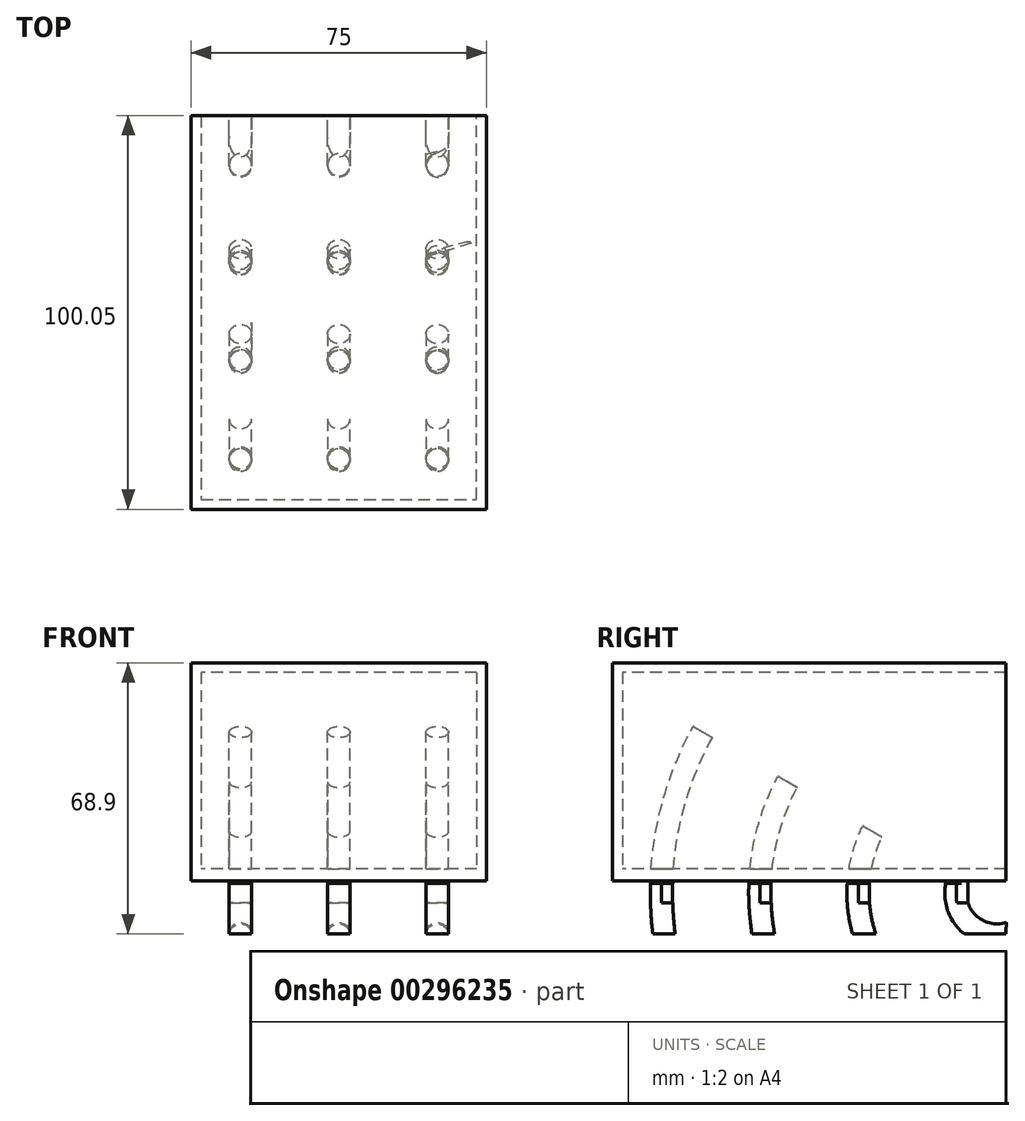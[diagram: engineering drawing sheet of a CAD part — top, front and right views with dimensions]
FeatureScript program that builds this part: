
annotation { "Feature Type Name" : "Feature", "Feature Type Description" : "" }
export const myFeature = defineFeature(function(context is Context, id is Id, definition is map)
    precondition{}
    {
        {
            var Q0;
            Q0=qCreatedBy(makeId("Top.planeOp"),FACE);
            var sketch = newSketch(context, id + "F0", { "sketchPlane" : qUnion([Q0])});
            skLineSegment(sketch, "E0.bottom", {"start": v(37.5, 50) * mm, "end": v(-37.5, 50) * mm});
            skLineSegment(sketch, "E0.top", {"start": v(37.5, -50) * mm, "end": v(-37.5, -50) * mm});
            skLineSegment(sketch, "E0.left", {"start": v(37.5, 50) * mm, "end": v(37.5, -50) * mm});
            skLineSegment(sketch, "E0.right", {"start": v(-37.5, 50) * mm, "end": v(-37.5, -50) * mm});
            skPoint(sketch, "E0.middle", {"position": v(0, 0) * mm});
            skSolve(sketch);
        }
        {
            var Q0;
            Q0 = qSketchRegion(id + "F0", true);
            extrude(context, id + "F1", {"entities" : qUnion([Q0]), "depth" : 3 * mm});
        }
        {
            var Q0;
            Q0=makeQuery(id+"F1.opExtrude","CAP_FACE",FACE,{"disambiguationData":[OSD([sQuery(id+"F0.wireOp",EDGE,"E0.bottom"),sQuery(id+"F0.wireOp",EDGE,"E0.top"),sQuery(id+"F0.wireOp",EDGE,"E0.left"),sQuery(id+"F0.wireOp",EDGE,"E0.right")])],"isStart":false});
            var sketch = newSketch(context, id + "F2", { "sketchPlane" : qUnion([Q0])});
            skLineSegment(sketch, "E1.top", {"start": v(-35, -47.5) * mm, "end": v(35, -47.5) * mm});
            skLineSegment(sketch, "E1.left", {"start": v(-35, 47.5) * mm, "end": v(-35, -47.5) * mm});
            skLineSegment(sketch, "E1.right", {"start": v(35, 47.5) * mm, "end": v(35, -47.5) * mm});
            skPoint(sketch, "E1.middle", {"position": v(0, 0) * mm});
            skLineSegment(sketch, "E2", {"start": v(-35, 47.5) * mm, "end": v(-35, 50) * mm});
            skLineSegment(sketch, "E3", {"start": v(35, 47.5) * mm, "end": v(35, 50) * mm});
            skLineSegment(sketch, "E4.bottom", {"start": v(-37.5, -50) * mm, "end": v(37.5, -50) * mm});
            skLineSegment(sketch, "E4.top", {"start": v(-37.5, 50) * mm, "end": v(37.5, 50) * mm});
            skLineSegment(sketch, "E4.left", {"start": v(-37.5, -50) * mm, "end": v(-37.5, 50) * mm});
            skLineSegment(sketch, "E4.right", {"start": v(37.5, -50) * mm, "end": v(37.5, 50) * mm});
            skSolve(sketch);
        }
        {
            var Q0;
            Q0=makeQuery(id+"F2.imprint","IMPRINT",FACE,{"disambiguationData":[TD([[makeQuery(id+"F2.imprint","IMPRINT",EDGE,{"derivedFrom":sQuery(id+"F2.wireOp",EDGE,"E1.top")}),-1.0]])]});
            extrude(context, id + "F3", {"entities" : qUnion([Q0]), "operationType" : NewBodyOperationType.ADD, "depth" : 50 * mm});
        }
        {
            var Q0;
            Q0=makeQuery(id+"F3.opExtrude","CAP_FACE",FACE,{"disambiguationData":[OSD([sQuery(id+"F2.wireOp",EDGE,"E1.top"),sQuery(id+"F2.wireOp",EDGE,"E1.left"),sQuery(id+"F2.wireOp",EDGE,"E1.right"),sQuery(id+"F2.wireOp",EDGE,"E2"),sQuery(id+"F2.wireOp",EDGE,"E3"),sQuery(id+"F2.wireOp",EDGE,"E4.bottom"),sQuery(id+"F2.wireOp",EDGE,"E4.top"),sQuery(id+"F2.wireOp",EDGE,"E4.left"),sQuery(id+"F2.wireOp",EDGE,"E4.right")])],"isStart":false});
            var sketch = newSketch(context, id + "F4", { "sketchPlane" : qUnion([Q0])});
            skLineSegment(sketch, "E5.bottom", {"start": v(-37.5, -50) * mm, "end": v(37.5, -50) * mm});
            skLineSegment(sketch, "E5.top", {"start": v(-37.5, 50) * mm, "end": v(37.5, 50) * mm});
            skLineSegment(sketch, "E5.left", {"start": v(-37.5, -50) * mm, "end": v(-37.5, 50) * mm});
            skLineSegment(sketch, "E5.right", {"start": v(37.5, -50) * mm, "end": v(37.5, 50) * mm});
            skSolve(sketch);
        }
        {
            var Q0;
            Q0 = qSketchRegion(id + "F4", true);
            extrude(context, id + "F5", {"entities" : qUnion([Q0]), "operationType" : NewBodyOperationType.ADD, "depth" : 2.4 * mm});
        }
        {
            var Q0;
            Q0=makeQuery(id+"F1.opExtrude","CAP_FACE",FACE,{"disambiguationData":[OSD([sQuery(id+"F0.wireOp",EDGE,"E0.bottom"),sQuery(id+"F0.wireOp",EDGE,"E0.top"),sQuery(id+"F0.wireOp",EDGE,"E0.left"),sQuery(id+"F0.wireOp",EDGE,"E0.right")])],"isStart":true});
            var sketch = newSketch(context, id + "F6", { "sketchPlane" : qUnion([Q0])});
            skLineSegment(sketch, "E6.bottom", {"start": v(37.5, -50) * mm, "end": v(-37.5, -50) * mm, "construction": true});
            skLineSegment(sketch, "E6.top", {"start": v(37.5, 50) * mm, "end": v(-37.5, 50) * mm, "construction": true});
            skLineSegment(sketch, "E6.left", {"start": v(37.5, -50) * mm, "end": v(37.5, 50) * mm, "construction": true});
            skLineSegment(sketch, "E6.right", {"start": v(-37.5, -50) * mm, "end": v(-37.5, 50) * mm, "construction": true});
            skLineSegment(sketch, "E7.bottom", {"start": v(-25, -37.5) * mm, "end": v(25, -37.5) * mm, "construction": true});
            skLineSegment(sketch, "E7.top", {"start": v(-25, 37.5) * mm, "end": v(25, 37.5) * mm, "construction": true});
            skLineSegment(sketch, "E7.left", {"start": v(-25, -37.5) * mm, "end": v(-25, 37.5) * mm, "construction": true});
            skLineSegment(sketch, "E7.right", {"start": v(25, -37.5) * mm, "end": v(25, 37.5) * mm, "construction": true});
            skPoint(sketch, "E7.middle", {"position": v(0, 0) * mm});
            skLineSegment(sketch, "E8", {"start": v(0, -52.67) * mm, "end": v(0, 62.06) * mm, "construction": true});
            skPoint(sketch, "E8.startSnap0", {"position": v(0, -50) * mm});
            skLineSegment(sketch, "E9", {"start": v(25, -12.5) * mm, "end": v(-25, -12.5) * mm, "construction": true});
            skLineSegment(sketch, "E10", {"start": v(25, 12.5) * mm, "end": v(-25, 12.5) * mm, "construction": true});
            skCircle(sketch, "E11", {"center": v(25, -37.5) * mm, "radius": 2.83 * mm});
            skCircle(sketch, "E12.MirrorC", {"center": v(-25, -37.5) * mm, "radius": 2.83 * mm});
            skCircle(sketch, "E13.MirrorC", {"center": v(25, 12.5) * mm, "radius": 2.83 * mm});
            skCircle(sketch, "E14.MirrorC", {"center": v(-25, 12.5) * mm, "radius": 2.83 * mm});
            skCircle(sketch, "E15", {"center": v(0, -37.5) * mm, "radius": 2.83 * mm});
            skCircle(sketch, "E16", {"center": v(0, -12.5) * mm, "radius": 2.83 * mm});
            skCircle(sketch, "E17", {"center": v(-25, -12.5) * mm, "radius": 2.83 * mm});
            skCircle(sketch, "E18", {"center": v(25, -12.5) * mm, "radius": 2.83 * mm});
            skCircle(sketch, "E19", {"center": v(25, 37.5) * mm, "radius": 2.83 * mm});
            skCircle(sketch, "E20", {"center": v(0, 37.5) * mm, "radius": 2.83 * mm});
            skCircle(sketch, "E21", {"center": v(0, 12.5) * mm, "radius": 2.83 * mm});
            skCircle(sketch, "E22", {"center": v(-25, 37.5) * mm, "radius": 2.83 * mm});
            skSolve(sketch);
        }
        {
            var Q0;
            Q0 = qSketchRegion(id + "F6", true);
            extrude(context, id + "F7", {"entities" : qUnion([Q0]), "operationType" : NewBodyOperationType.ADD, "depth" : 5.6 * mm});
        }
        {
            var Q0;
            Q0=makeQuery(id+"F5.boolean.opBoolean","MERGE",FACE,{"derivedFrom":[makeQuery(id+"F3.boolean.opBoolean","MERGE",FACE,{"derivedFrom":[makeQuery(id+"F1.opExtrude","SWEPT_FACE",FACE,{"disambiguationData":[OSD([sQuery(id+"F0.wireOp",EDGE,"E0.right")])]}),makeQuery(id+"F3.opExtrude","SWEPT_FACE",FACE,{"disambiguationData":[OSD([sQuery(id+"F2.wireOp",EDGE,"E4.left")])]})]}),makeQuery(id+"F5.opExtrude","SWEPT_FACE",FACE,{"disambiguationData":[OSD([sQuery(id+"F4.wireOp",EDGE,"E5.left")])]})]});
            var sketch = newSketch(context, id + "F8", { "sketchPlane" : qUnion([Q0])});
            skLineSegment(sketch, "E23.bottom", {"start": v(-50, 0) * mm, "end": v(50, 0) * mm});
            skLineSegment(sketch, "E23.top", {"start": v(-50, 55.4) * mm, "end": v(50, 55.4) * mm});
            skLineSegment(sketch, "E23.left", {"start": v(-50, 0) * mm, "end": v(-50, 55.4) * mm});
            skLineSegment(sketch, "E23.right", {"start": v(50, 0) * mm, "end": v(50, 55.4) * mm});
            skPoint(sketch, "E24.end.orphan", {"position": v(-50, -13.6) * mm});
            skPoint(sketch, "E25.start.orphan", {"position": v(-37.5, 0) * mm});
            skArc(sketch, "E26", {"start": v(-50, -13.6) * mm, "mid": v(-39.85, -10.39) * mm, "end": v(-37.5, 0) * mm});
            skSolve(sketch);
        }
        {
            var Q0;
            Q0=makeQuery(id+"F7.opExtrude","CAP_FACE",FACE,{"disambiguationData":[OSD([sQuery(id+"F6.wireOp",EDGE,"E12.MirrorC")])],"isStart":false});
            var Q1;
            Q1=makeQuery(id+"F7.opExtrude","CAP_FACE",FACE,{"disambiguationData":[OSD([sQuery(id+"F6.wireOp",EDGE,"E17")])],"isStart":false});
            var Q2;
            Q2=makeQuery(id+"F7.opExtrude","CAP_FACE",FACE,{"disambiguationData":[OSD([sQuery(id+"F6.wireOp",EDGE,"E16")])],"isStart":false});
            var Q3;
            Q3=makeQuery(id+"F7.opExtrude","CAP_FACE",FACE,{"disambiguationData":[OSD([sQuery(id+"F6.wireOp",EDGE,"E18")])],"isStart":false});
            var Q4;
            Q4=makeQuery(id+"F7.opExtrude","CAP_FACE",FACE,{"disambiguationData":[OSD([sQuery(id+"F6.wireOp",EDGE,"E15")])],"isStart":false});
            var Q5;
            Q5=makeQuery(id+"F7.opExtrude","CAP_FACE",FACE,{"disambiguationData":[OSD([sQuery(id+"F6.wireOp",EDGE,"E11")])],"isStart":false});
            var Q6;
            Q6=makeQuery(id+"F7.opExtrude","CAP_FACE",FACE,{"disambiguationData":[OSD([sQuery(id+"F6.wireOp",EDGE,"E13.MirrorC")])],"isStart":false});
            var Q7;
            Q7=makeQuery(id+"F7.opExtrude","CAP_FACE",FACE,{"disambiguationData":[OSD([sQuery(id+"F6.wireOp",EDGE,"E21")])],"isStart":false});
            var Q8;
            Q8=makeQuery(id+"F7.opExtrude","CAP_FACE",FACE,{"disambiguationData":[OSD([sQuery(id+"F6.wireOp",EDGE,"E14.MirrorC")])],"isStart":false});
            var Q9;
            Q9=makeQuery(id+"F7.opExtrude","CAP_FACE",FACE,{"disambiguationData":[OSD([sQuery(id+"F6.wireOp",EDGE,"E22")])],"isStart":false});
            var Q10;
            Q10=makeQuery(id+"F7.opExtrude","CAP_FACE",FACE,{"disambiguationData":[OSD([sQuery(id+"F6.wireOp",EDGE,"E20")])],"isStart":false});
            var Q11;
            Q11=makeQuery(id+"F7.opExtrude","CAP_FACE",FACE,{"disambiguationData":[OSD([sQuery(id+"F6.wireOp",EDGE,"E19")])],"isStart":false});
            var Q12;
            Q12=sQuery(id+"F8.wireOp",EDGE,"E26");
            sweep(context, id + "F9", {"operationType" : NewBodyOperationType.ADD, "profiles" : qUnion([Q0, Q1, Q2, Q3, Q4, Q5, Q6, Q7, Q8, Q9, Q10, Q11]), "path" : qUnion([Q12])});
        }
        {
            var Q0;
            Q0=makeQuery(id+"F5.boolean.opBoolean","MERGE",FACE,{"derivedFrom":[makeQuery(id+"F3.boolean.opBoolean","MERGE",FACE,{"derivedFrom":[makeQuery(id+"F1.opExtrude","SWEPT_FACE",FACE,{"disambiguationData":[OSD([sQuery(id+"F0.wireOp",EDGE,"E0.right")])]}),makeQuery(id+"F3.opExtrude","SWEPT_FACE",FACE,{"disambiguationData":[OSD([sQuery(id+"F2.wireOp",EDGE,"E4.left")])]})]}),makeQuery(id+"F5.opExtrude","SWEPT_FACE",FACE,{"disambiguationData":[OSD([sQuery(id+"F4.wireOp",EDGE,"E5.left")])]})]});
            var sketch = newSketch(context, id + "F10", { "sketchPlane" : qUnion([Q0])});
            skLineSegment(sketch, "E27.bottom", {"start": v(-50, 55.4) * mm, "end": v(50, 55.4) * mm});
            skLineSegment(sketch, "E27.top", {"start": v(-50, 0) * mm, "end": v(50, 0) * mm});
            skLineSegment(sketch, "E27.left", {"start": v(-50, 55.4) * mm, "end": v(-50, 0) * mm});
            skLineSegment(sketch, "E27.right", {"start": v(50, 55.4) * mm, "end": v(50, 0) * mm});
            skLineSegment(sketch, "E28.bottom", {"start": v(50, 55.4) * mm, "end": v(-56.53, 55.4) * mm});
            skLineSegment(sketch, "E28.top", {"start": v(50, -13.5) * mm, "end": v(-56.53, -13.5) * mm});
            skLineSegment(sketch, "E28.left", {"start": v(50, 55.4) * mm, "end": v(50, -13.5) * mm});
            skLineSegment(sketch, "E28.right", {"start": v(-56.53, 55.4) * mm, "end": v(-56.53, -13.5) * mm});
            skLineSegment(sketch, "E29.bottom", {"start": v(-56.53, -13.5) * mm, "end": v(62.28, -13.5) * mm});
            skLineSegment(sketch, "E29.top", {"start": v(-56.53, -126.45) * mm, "end": v(62.28, -126.45) * mm});
            skLineSegment(sketch, "E29.left", {"start": v(-56.53, -13.5) * mm, "end": v(-56.53, -126.45) * mm});
            skLineSegment(sketch, "E29.right", {"start": v(62.28, -13.5) * mm, "end": v(62.28, -126.45) * mm});
            skLineSegment(sketch, "E30.bottom", {"start": v(62.28, -13.5) * mm, "end": v(-107.86, -13.5) * mm});
            skLineSegment(sketch, "E30.top", {"start": v(62.28, -126.45) * mm, "end": v(-107.86, -126.45) * mm});
            skLineSegment(sketch, "E30.right", {"start": v(-107.86, -13.5) * mm, "end": v(-107.86, -126.45) * mm});
            skSolve(sketch);
        }
        {
            var Q0;
            {var subQ0=sQuery(id+"F10.wireOp",EDGE,"E29.left");Q0=makeQuery(id+"F10.imprint","IMPRINT",FACE,{"disambiguationData":[TD([[makeQuery(id+"F10.imprint","IMPRINT",EDGE,{"derivedFrom":subQ0}),-1.0]])]});}
            var Q1;
            {var subQ1=sQuery(id+"F10.wireOp",EDGE,"E29.left");Q1=makeQuery(id+"F10.imprint","IMPRINT",FACE,{"disambiguationData":[TD([[makeQuery(id+"F10.imprint","IMPRINT",EDGE,{"derivedFrom":subQ1}),1.0]])]});}
            extrude(context, id + "F11", {"entities" : qUnion([Q0, Q1]), "operationType" : NewBodyOperationType.REMOVE, "endBound" : BoundingType.THROUGH_ALL, "oppositeDirection" : true, "depth" : 25 * mm});
        }
    });
